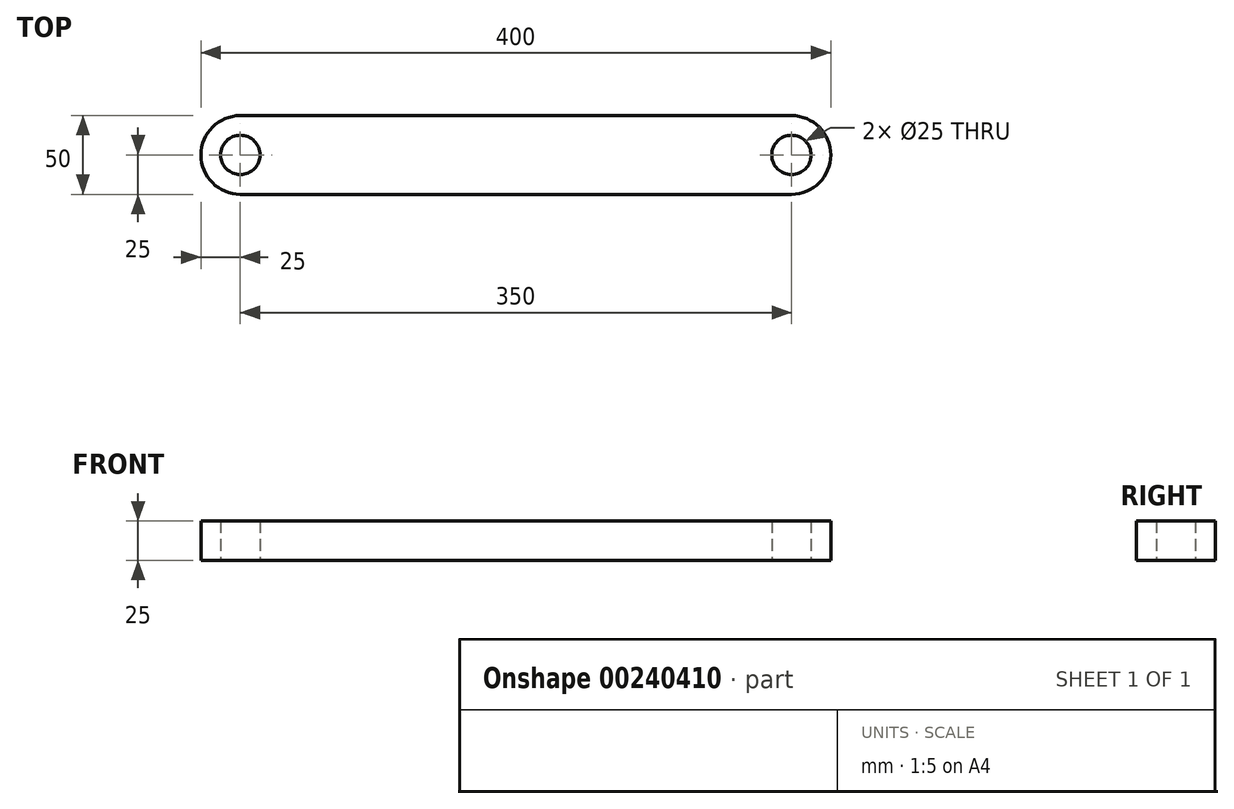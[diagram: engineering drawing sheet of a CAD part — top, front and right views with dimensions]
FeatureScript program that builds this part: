
annotation { "Feature Type Name" : "Feature", "Feature Type Description" : "" }
export const myFeature = defineFeature(function(context is Context, id is Id, definition is map)
    precondition{}
    {
        {
            var Q0;
            Q0=qCreatedBy(makeId("Top.planeOp"),FACE);
            var sketch = newSketch(context, id + "F0", { "sketchPlane" : qUnion([Q0])});
            skLineSegment(sketch, "E0.rect.bottom", {"start": v(175, 25) * mm, "end": v(-175, 25) * mm});
            skLineSegment(sketch, "E0.rect.top", {"start": v(175, -25) * mm, "end": v(-175, -25) * mm});
            skPoint(sketch, "E0.rect.middle", {"position": v(0, 0) * mm});
            skArc(sketch, "E1", {"start": v(-175, 25) * mm, "mid": v(-200, 0) * mm, "end": v(-175, -25) * mm});
            skCircle(sketch, "E2", {"center": v(-175, 0) * mm, "radius": 12.5 * mm});
            skArc(sketch, "E3", {"start": v(175, -25) * mm, "mid": v(200, 0) * mm, "end": v(175, 25) * mm});
            skCircle(sketch, "E4", {"center": v(175, 0) * mm, "radius": 12.5 * mm});
            skSolve(sketch);
        }
        {
            var Q0;
            Q0=qSketchRegion(id+"F0",true);
            extrude(context, id + "F1", {"entities" : qUnion([Q0]), "depth" : 25 * mm});
        }
    });
